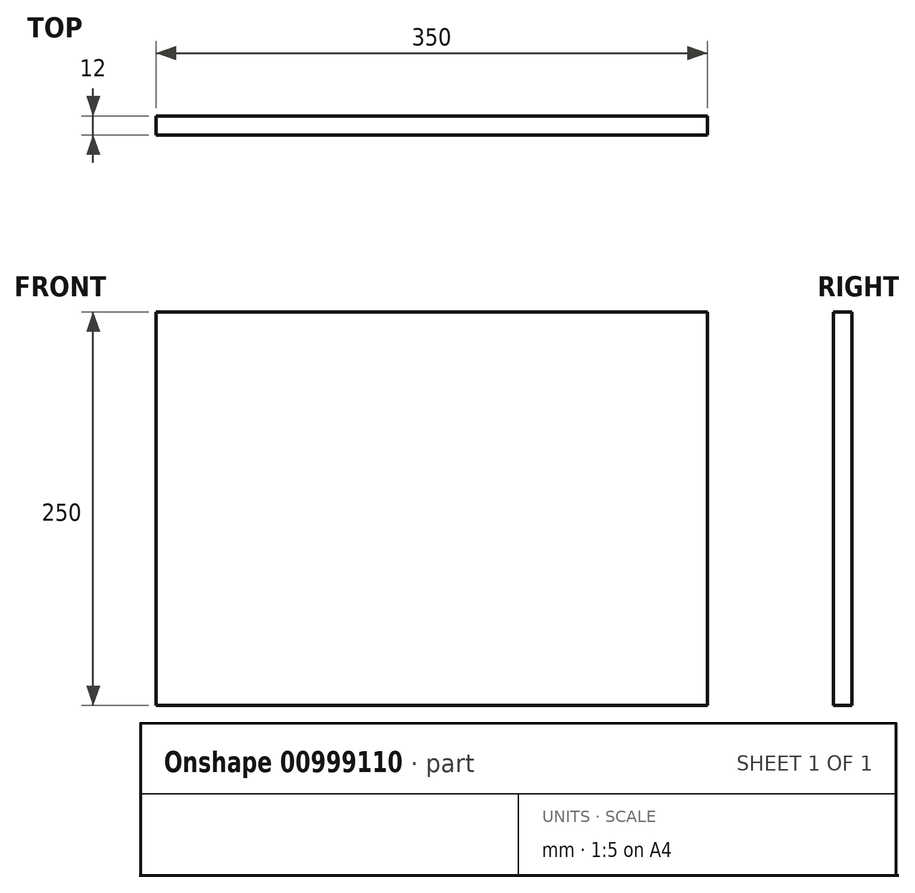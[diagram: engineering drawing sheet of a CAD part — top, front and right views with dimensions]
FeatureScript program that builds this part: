
annotation { "Feature Type Name" : "Feature", "Feature Type Description" : "" }
export const myFeature = defineFeature(function(context is Context, id is Id, definition is map)
    precondition{}
    {
        {
            var Q0;
            Q0=qCreatedBy(makeId("Front.planeOp"),FACE);
            var sketch = newSketch(context, id + "F0", { "sketchPlane" : qUnion([Q0])});
            skLineSegment(sketch, "E0.bottom", {"start": v(-175, -125) * mm, "end": v(175, -125) * mm});
            skLineSegment(sketch, "E0.top", {"start": v(-175, 125) * mm, "end": v(175, 125) * mm});
            skLineSegment(sketch, "E0.left", {"start": v(-175, -125) * mm, "end": v(-175, 125) * mm});
            skLineSegment(sketch, "E0.right", {"start": v(175, -125) * mm, "end": v(175, 125) * mm});
            skPoint(sketch, "E0.middle", {"position": v(0, 0) * mm});
            skSolve(sketch);
        }
        {
            var Q0;
            Q0=makeQuery(id+"F0.imprint","IMPRINT",FACE,{"disambiguationData":[TD([[makeQuery(id+"F0.imprint","IMPRINT",EDGE,{"derivedFrom":sQuery(id+"F0.wireOp",EDGE,"E0.bottom")}),1.0]])]});
            extrude(context, id + "F1", {"entities" : qUnion([Q0]), "depth" : 12 * mm, "offsetDistance" : 25 * mm});
        }
    });
